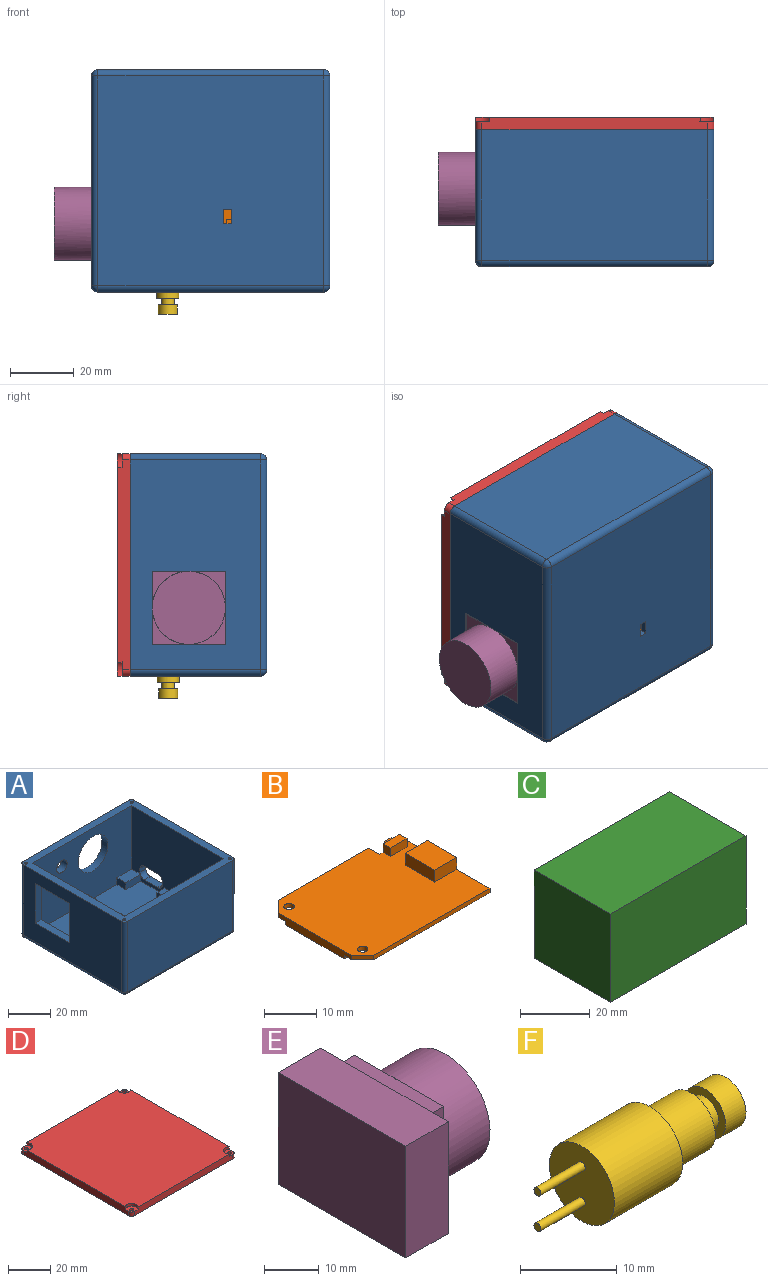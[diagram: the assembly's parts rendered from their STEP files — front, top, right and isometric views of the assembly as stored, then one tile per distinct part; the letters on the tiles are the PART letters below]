
ASSEMBLY  parts=6 mates=6
PART A: 66 faces, bbox 75x70x43 mm
  f0: plane 66x41mm, normal (-1,0,0), area 2177mm2, adj f2,f41,f42,f43,f44,f47,f53,f56
  f1: plane 62x41mm, normal (1,0,0), area 2013mm2, adj f2,f3,f9,f10,f41,f42,f43,f44
  f2: plane 75x70mm, normal (0,0,1), area 1084.5mm2, adj f0,f1,f5,f6,f7,f8,f9,f10
  f3: plane 67x62mm, normal (0,0,1), area 4005.2mm2, adj f1,f5,f9,f10,f19,f20,f21,f23
  f4: plane 71x66mm, normal (0,0,-1), area 4674.8mm2, adj f36,f37,f38,f39,f48,f49,f53,f54
  f5: plane 62x41mm, normal (-1,0,0), area 2385.8mm2, adj f2,f3,f9,f10,f11,f12,f13,f14
  f6: plane 66x41mm, normal (1,0,0), area 2593.7mm2, adj f2,f11,f12,f13,f14,f15,f16,f17
  f7: plane 71x41mm, normal (0,1,0), area 2558.4mm2, adj f2,f40,f50,f54,f56,f65
  f8: plane 71x41mm, normal (0,-1,0), area 2911mm2, adj f2,f45,f47,f48
  f9: plane 67x41mm, normal (0,-1,0), area 2334.4mm2, adj f1,f2,f3,f5,f28,f30,f31,f34
  f10: plane 67x41mm, normal (0,1,0), area 2747mm2, adj f1,f2,f3,f5
  f11: plane 9x4mm, normal (0,0,-1), area 36mm2, adj f5,f6,f15,f18
  f12: plane 4x2mm, normal (0,1,0), area 8mm2, adj f5,f6,f15,f16
  f13: plane 9x4mm, normal (0,0,1), area 36mm2, adj f5,f6,f16,f17
  f14: plane 4x2mm, normal (0,-1,0), area 8mm2, adj f5,f6,f17,f18
  f15: cylinder r=3mm len=4mm, axis (1,0,0), area 18.8mm2, adj f5,f6,f11,f12
  f16: cylinder r=3mm len=4mm, axis (-1,0,0), area 18.8mm2, adj f5,f6,f12,f13
  f17: cylinder r=3mm len=4mm, axis (1,0,0), area 18.8mm2, adj f5,f6,f13,f14,f33
  f18: cylinder r=3mm len=4mm, axis (-1,0,0), area 18.8mm2, adj f5,f6,f11,f14
  f19: plane 5x4mm, normal (0,-1,0), area 20mm2, adj f3,f5,f21,f22
  f20: plane 5x4mm, normal (0,1,0), area 20mm2, adj f3,f5,f21,f22
  f21: plane 5x4mm, normal (-1,0,0), area 20mm2, adj f3,f19,f20,f22
  f22: plane 5x5mm, normal (0,0,1), area 25mm2, adj f5,f19,f20,f21
  f23: plane 5x4mm, normal (0,1,0), area 20mm2, adj f3,f24,f26,f27
  f24: plane 5x4mm, normal (-1,0,0), area 20mm2, adj f3,f23,f25,f27
  f25: plane 5x4mm, normal (0,-1,0), area 20mm2, adj f3,f24,f26,f27
  f26: plane 5x4mm, normal (1,0,0), area 20mm2, adj f3,f23,f25,f27
  f27: plane 5x5mm, normal (0,0,1), area 25mm2, adj f23,f24,f25,f26
  f28: plane 5.5x4mm, normal (-1,0,0), area 22mm2, adj f3,f9,f29,f31
  f29: plane 5x4mm, normal (0,-1,0), area 20mm2, adj f3,f28,f30,f31
  f30: plane 5.5x4mm, normal (1,0,0), area 22mm2, adj f3,f9,f29,f31
  f31: plane 5.5x5mm, normal (0,0,1), area 27.5mm2, adj f9,f28,f29,f30
  f32: plane 10x4mm, normal (0,-1,0), area 40mm2, adj f3,f5,f33,f34,f35
  f33: plane 0.66x0.33mm, normal (1,0,0), area 0.1mm2, adj f17,f32,f35
  f34: plane 6x4mm, normal (-1,0,0), area 24mm2, adj f3,f9,f32,f35
  f35: plane 10x6mm, normal (0,0,1), area 60mm2, adj f5,f9,f32,f33,f34
  f36: plane 4.5x2mm, normal (1,0,0), area 9mm2, adj f3,f4,f37,f39
  f37: plane 2.5x2mm, normal (0,1,0), area 5mm2, adj f3,f4,f36,f38
  f38: plane 4.5x2mm, normal (-1,0,0), area 9mm2, adj f3,f4,f37,f39
  f39: plane 2.5x2mm, normal (0,-1,0), area 5mm2, adj f3,f4,f36,f38
  f40: cylinder r=3.5mm len=7mm, axis (0,1,0), area 88mm2, adj f7,f9
  f41: plane 23x4mm, normal (0,1,0), area 92mm2, adj f0,f1,f42,f44
  f42: plane 23x4mm, normal (0,0,-1), area 92mm2, adj f0,f1,f41,f43
  f43: plane 23x4mm, normal (0,-1,0), area 92mm2, adj f0,f1,f42,f44
  f44: plane 23x4mm, normal (0,0,1), area 92mm2, adj f0,f1,f41,f43
  f45: cylinder r=2mm len=41mm, axis (0,0,1), area 128.8mm2, adj f2,f6,f8,f46
  f46: sphere r=2mm, area 6.3mm2, adj f45,f48,f49
  f47: cylinder r=2mm len=41mm, axis (0,0,-1), area 128.8mm2, adj f0,f2,f8,f51
  f48: cylinder r=2mm len=71mm, axis (1,0,0), area 223.1mm2, adj f4,f8,f46,f51
  f49: cylinder r=2mm len=66mm, axis (0,1,0), area 207.3mm2, adj f4,f6,f46,f52
  f50: cylinder r=2mm len=41mm, axis (0,0,-1), area 128.8mm2, adj f2,f6,f7,f52
  f51: sphere r=2mm, area 6.3mm2, adj f47,f48,f53
  f52: sphere r=2mm, area 6.3mm2, adj f49,f50,f54
  f53: cylinder r=2mm len=66mm, axis (0,-1,0), area 207.3mm2, adj f0,f4,f51,f55
  f54: cylinder r=2mm len=71mm, axis (-1,0,0), area 223.1mm2, adj f4,f7,f52,f55
  f55: sphere r=2mm, area 6.3mm2, adj f53,f54,f56
  f56: cylinder r=2mm len=41mm, axis (0,0,1), area 128.8mm2, adj f0,f2,f7,f55
  f57: cylinder r=0.8mm len=10mm, axis (0,0,1), area 50.3mm2, adj f2,f58
  f58: plane 1.6x1.6mm, normal (0,0,1), area 2mm2, adj f57
  f59: cylinder r=0.8mm len=10mm, axis (0,0,1), area 50.3mm2, adj f2,f60
  f60: plane 1.6x1.6mm, normal (0,0,1), area 2mm2, adj f59
  f61: cylinder r=0.8mm len=10mm, axis (0,0,1), area 50.3mm2, adj f2,f62
  f62: plane 1.6x1.6mm, normal (0,0,1), area 2mm2, adj f61
  f63: cylinder r=0.8mm len=10mm, axis (0,0,1), area 50.3mm2, adj f2,f64
  f64: plane 1.6x1.6mm, normal (0,0,1), area 2mm2, adj f63
  f65: cylinder r=10mm len=20mm, axis (0,1,0), area 251.3mm2, adj f7,f9
PART B: 33 faces, bbox 34.5x26x4.6 mm
  f0: plane 34.5x26mm, normal (0,0,-1), area 758.7mm2, adj f2,f3,f4,f5,f6,f7,f8,f9
  f1: plane 34.5x26mm, normal (0,0,1), area 803.7mm2, adj f2,f3,f4,f5,f6,f7,f8,f9
  f2: plane 23x3.8mm, normal (1,0,0), area 45.4mm2, adj f0,f1,f5,f10,f11,f13,f14
  f3: plane 24.5x1mm, normal (0,1,0), area 24.5mm2, adj f0,f1,f6,f15
  f4: plane 20x1.8mm, normal (-1,0,0), area 32.8mm2, adj f0,f1,f6,f7,f25,f27,f28
  f5: plane 31.5x1mm, normal (0,-1,0), area 31.5mm2, adj f0,f1,f2,f7
  f6: plane 3x3mm, normal (-0.71,0.71,0), area 4.2mm2, adj f0,f1,f3,f4
  f7: plane 3x3mm, normal (-0.71,-0.71,0), area 4.2mm2, adj f0,f1,f4,f5
  f8: cylinder r=1mm len=2mm, axis (0,0,1), area 6.3mm2, adj f0,f1
  f9: cylinder r=1mm len=2mm, axis (0,0,1), area 6.3mm2, adj f0,f1
  f10: plane 6x2.8mm, normal (0,-1,0), area 16.8mm2, adj f1,f2,f12,f13
  f11: plane 6x2.8mm, normal (0,1,0), area 16.8mm2, adj f1,f2,f12,f13
  f12: plane 8x2.8mm, normal (-1,0,0), area 22.4mm2, adj f1,f10,f11,f13
  f13: plane 8x6mm, normal (0,0,1), area 48mm2, adj f2,f10,f11,f12
  f14: plane 7x3mm, normal (0,1,0), area 14mm2, adj f0,f1,f2,f15,f16,f17,f19,f20
  f15: plane 3x1mm, normal (1,0,0), area 3mm2, adj f0,f1,f3,f14
  f16: plane 2x2mm, normal (1,0,0), area 4mm2, adj f1,f14,f18,f19
  f17: plane 2x2mm, normal (-1,0,0), area 4mm2, adj f1,f14,f18,f19
  f18: plane 4.5x2mm, normal (0,-1,0), area 9mm2, adj f1,f16,f17,f19
  f19: plane 4.5x2mm, normal (0,0,1), area 9mm2, adj f14,f16,f17,f18
  f20: plane 1.8x1mm, normal (0,0,1), area 1.8mm2, adj f14,f21,f23,f24
  f21: plane 1.1x1mm, normal (1,0,0), area 1.1mm2, adj f14,f20,f22,f24
  f22: plane 1.8x1mm, normal (0,0,-1), area 1.8mm2, adj f14,f21,f23,f24
  f23: plane 1.1x1mm, normal (-1,0,0), area 1.1mm2, adj f14,f20,f22,f24
  f24: plane 1.8x1.1mm, normal (0,1,0), area 1.8mm2, adj f20,f21,f22,f23,f29
  f25: plane 6x0.8mm, normal (0,1,0), area 4.8mm2, adj f0,f4,f26,f28
  f26: plane 13x0.8mm, normal (1,0,0), area 10.4mm2, adj f0,f25,f28,f31
  f27: plane 8x0.8mm, normal (0,-1,0), area 6.4mm2, adj f0,f4,f28,f32
  f28: plane 16x8mm, normal (0,0,-1), area 102mm2, adj f4,f25,f26,f27,f31,f32
  f29: cylinder r=0.25mm len=0.5mm, axis (0,-1,0), area 0.2mm2, adj f24,f30
  f30: plane 0.5x0.5mm, normal (0,1,0), area 0.2mm2, adj f29
  f31: plane 2x0.8mm, normal (0,1,0), area 1.6mm2, adj f0,f26,f28,f32
  f32: plane 3x0.8mm, normal (1,0,0), area 2.4mm2, adj f0,f27,f28,f31
PART C: 6 faces, bbox 55x31x31 mm
  f0: plane 55x31mm, normal (0,1,0), area 1705mm2, adj f1,f3,f4,f5
  f1: plane 31x31mm, normal (-1,0,0), area 961mm2, adj f0,f2,f4,f5
  f2: plane 55x31mm, normal (0,-1,0), area 1705mm2, adj f1,f3,f4,f5
  f3: plane 31x31mm, normal (1,0,0), area 961mm2, adj f0,f2,f4,f5
  f4: plane 55x31mm, normal (0,0,1), area 1705mm2, adj f0,f1,f2,f3
  f5: plane 55x31mm, normal (0,0,-1), area 1705mm2, adj f0,f1,f2,f3
PART D: 22 faces, bbox 70x75x4 mm
  f0: cylinder r=2mm len=2.5mm, axis (0,0,1), area 7.9mm2, adj f4,f5,f9,f17
  f1: cylinder r=2mm len=2.5mm, axis (0,0,-1), area 7.9mm2, adj f5,f6,f9,f15
  f2: cylinder r=2mm len=2.5mm, axis (0,0,1), area 7.9mm2, adj f6,f7,f9,f13
  f3: cylinder r=2mm len=2.5mm, axis (0,0,-1), area 7.9mm2, adj f4,f7,f9,f11
  f4: plane 66x4mm, normal (0,1,0), area 257.3mm2, adj f0,f3,f8,f9,f10,f11,f16,f17
  f5: plane 71x4mm, normal (-1,0,0), area 277.3mm2, adj f0,f1,f8,f9,f14,f15,f16,f17
  f6: plane 66x4mm, normal (0,-1,0), area 257.3mm2, adj f1,f2,f8,f9,f12,f13,f14,f15
  f7: plane 71x4mm, normal (1,0,0), area 277.3mm2, adj f2,f3,f8,f9,f10,f11,f12,f13
  f8: plane 75x70mm, normal (0,0,1), area 5161.6mm2, adj f4,f5,f6,f7,f10,f12,f14,f16
  f9: plane 75x70mm, normal (0,0,-1), area 5234mm2, adj f0,f1,f2,f3,f4,f5,f6,f7
  f10: cylinder r=3mm len=5mm, axis (0,0,1), area 13.6mm2, adj f4,f7,f8,f11
  f11: plane 5x5mm, normal (0,0,1), area 18.1mm2, adj f3,f4,f7,f10,f21
  f12: cylinder r=3mm len=5mm, axis (0,0,1), area 13.6mm2, adj f6,f7,f8,f13
  f13: plane 5x5mm, normal (0,0,1), area 18.1mm2, adj f2,f6,f7,f12,f20
  f14: cylinder r=3mm len=5mm, axis (0,0,1), area 13.6mm2, adj f5,f6,f8,f15
  f15: plane 5x5mm, normal (0,0,1), area 18.1mm2, adj f1,f5,f6,f14,f19
  f16: cylinder r=3mm len=5mm, axis (0,0,1), area 13.6mm2, adj f4,f5,f8,f17
  f17: plane 5x5mm, normal (0,0,1), area 18.1mm2, adj f0,f4,f5,f16,f18
  f18: cylinder r=1mm len=2.5mm, axis (0,0,1), area 15.7mm2, adj f9,f17
  f19: cylinder r=1mm len=2.5mm, axis (0,0,1), area 15.7mm2, adj f9,f15
  f20: cylinder r=1mm len=2.5mm, axis (0,0,1), area 15.7mm2, adj f9,f13
  f21: cylinder r=1mm len=2.5mm, axis (0,0,1), area 15.7mm2, adj f9,f11
PART E: 16 faces, bbox 26.8x33x25 mm
  f0: plane 11.5x11.5mm, normal (1,0,0), area 28.4mm2, adj f11,f12,f14
  f1: plane 11.5x11.5mm, normal (1,0,0), area 28.4mm2, adj f9,f12,f14
  f2: plane 11.5x11.5mm, normal (1,0,0), area 28.4mm2, adj f9,f10,f14
  f3: plane 33x25mm, normal (1,0,0), area 296mm2, adj f4,f5,f6,f7,f9,f10,f11,f12
  f4: plane 25x11mm, normal (0,1,0), area 275mm2, adj f3,f5,f7,f8
  f5: plane 33x11mm, normal (0,0,1), area 363mm2, adj f3,f4,f6,f8
  f6: plane 25x11mm, normal (0,-1,0), area 275mm2, adj f3,f5,f7,f8
  f7: plane 33x11mm, normal (0,0,-1), area 363mm2, adj f3,f4,f6,f8
  f8: plane 33x25mm, normal (-1,0,0), area 825mm2, adj f4,f5,f6,f7
  f9: plane 23x3.8mm, normal (0,0,1), area 87.4mm2, adj f1,f2,f3,f10,f12
  f10: plane 23x3.8mm, normal (0,-1,0), area 87.4mm2, adj f2,f3,f9,f11,f13
  f11: plane 23x3.8mm, normal (0,0,-1), area 87.4mm2, adj f0,f3,f10,f12,f13
  f12: plane 23x3.8mm, normal (0,1,0), area 87.4mm2, adj f0,f1,f3,f9,f11
  f13: plane 11.5x11.5mm, normal (1,0,0), area 28.4mm2, adj f10,f11,f14
  f14: cylinder r=11.5mm len=23mm, axis (-1,0,0), area 867.1mm2, adj f0,f1,f2,f13,f15
  f15: plane 23x23mm, normal (1,0,0), area 415.5mm2, adj f14
PART F: 13 faces, bbox 27.5x9.5x9.5 mm
  f0: cylinder r=3.5mm len=7mm, axis (-1,0,0), area 131.9mm2, adj f1,f8
  f1: plane 7x7mm, normal (1,0,0), area 25.9mm2, adj f0,f2
  f2: cylinder r=2mm len=4mm, axis (-1,0,0), area 25.1mm2, adj f1,f5
  f3: cylinder r=3mm len=6mm, axis (-1,0,0), area 56.5mm2, adj f4,f5
  f4: plane 6x6mm, normal (1,0,0), area 28.3mm2, adj f3
  f5: plane 6x6mm, normal (-1,0,0), area 15.7mm2, adj f2,f3
  f6: cylinder r=4.75mm len=10mm, axis (1,0,0), area 298.5mm2, adj f7,f8
  f7: plane 9.5x9.5mm, normal (-1,0,0), area 69.3mm2, adj f6,f9,f11
  f8: plane 9.5x9.5mm, normal (1,0,0), area 32.4mm2, adj f0,f6
  f9: cylinder r=0.5mm len=6.5mm, axis (1,0,0), area 20.4mm2, adj f7,f10
  f10: plane 1x1mm, normal (-1,0,0), area 0.8mm2, adj f9
  f11: cylinder r=0.5mm len=6.5mm, axis (1,0,0), area 20.4mm2, adj f7,f12
  f12: plane 1x1mm, normal (-1,0,0), area 0.8mm2, adj f11
PLACE A rot(axis=(-1,0,0),90deg) t=(3.7,-18.71,14.37)mm
PLACE B rot(axis=(-1,0,0),90deg) t=(-4.32,-12.71,-6.01)mm
PLACE C t=(3.09,24.85,30.84)mm
PLACE D rot(axis=(-0.58,0.58,0.58),120deg) t=(-2.8,24.29,16.37)mm
PLACE E rot(axis=(0,0.71,-0.71),180deg) t=(-14.8,2.65,27.65)mm
PLACE F rot(axis=(0,1,0),90deg) t=(-5.8,12.29,0.37)mm
MATE fastened E.f11 <-> A.f42  axis (0,-1,0) through (-25.8,17.29,29.37)mm
MATE planar B.f0 <-> A.f31  axis (0,-1,0) through (25.76,-12.71,14.64)mm
MATE fastened D.f2 <-> A.f50  axis (0,-1,0) through (43.2,24.29,-1.63)mm
MATE fastened F.f0 <-> A.f40  axis (0,0,1) through (-5.8,12.29,0.37)mm
MATE fastened B.f0 <-> A.f22  axis (0,1,0) through (41.2,-12.71,27.37)mm
MATE planar C.f2 <-> A.f3  axis (0,-1,0) through (13.17,-16.71,46.34)mm
